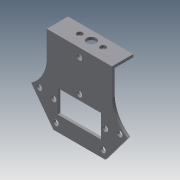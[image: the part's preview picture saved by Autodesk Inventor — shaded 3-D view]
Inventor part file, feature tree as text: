
AUTODESK INVENTOR PART (.ipt)
format: ipt  version: 2013 (Build 170138000, 138)  size: 1,052,160 bytes
history: native  units: mm
features: sketch x94, extrude x83, fillet x2
ambient origin geometry x8: Origin, YZ Plane, XZ Plane, XY Plane, X Axis, Y Axis, Z Axis, Center Point
bodies: Solid1 (feature_tree)
feature tree (179):
  extrude  "Extrusion1"  Depth=10.0mm
  extrude  "Extrusion2"  Depth=10.0mm
  sketch  "Sketch3"  dims[d8=2.0mm d9=0.0mm d11=3.0mm]
  extrude  "Extrusion3"  Depth=3.0mm
  extrude  "Extrusion4"  Depth=3.0mm
  extrude  "Extrusion5"  Depth=10.0mm TaperAngle=0.0deg
  extrude  "Extrusion6"  Depth=3.0mm
  sketch  "Sketch8"  dims[d24=10.0mm d25=0.0mm d26=2.0mm d27=0.0mm]
  extrude  "Extrusion7"  Depth=3.0mm
  extrude  "Extrusion8"  Depth=2.0mm TaperAngle=0.0deg
  extrude  "Extrusion9"  Depth=3.0mm
  extrude  "Extrusion10"  Depth=2.0mm TaperAngle=0.0deg
  extrude  "Extrusion11"  Depth=4.0mm
  extrude  "Extrusion12"  Depth=4.0mm
  extrude  "Extrusion13"  Depth=1.8mm
  sketch  "Sketch16"  dims[d61=4.0mm d62=4.0mm]
  extrude  "Extrusion14"  Depth=4.0mm
  extrude  "Extrusion15"  Depth=12.0mm
  extrude  "Extrusion16"  Depth=4.0mm
  extrude  "Extrusion17"  Depth=16.0mm
  sketch  "Sketch21"  dims[d75=30.0mm d77=2.0mm d78=0.0mm]
  extrude  "Extrusion18"  Depth=10.4mm
  extrude  "Extrusion19"  Depth=4.0mm
  extrude  "Extrusion20"  Depth=20.0mm
  extrude  "Extrusion21"  Depth=2.0mm TaperAngle=0.0deg
  extrude  "Extrusion22"  Depth=2.3mm
  extrude  "Extrusion23"  Depth=24.0mm
  extrude  "Extrusion24"  Depth=2.0mm TaperAngle=0.0deg
  extrude  "Extrusion25"  Depth=3.0mm
  extrude  "Extrusion26"  Depth=2.0mm TaperAngle=0.0deg
  extrude  "Extrusion27"  Depth=2.0mm TaperAngle=0.0deg
  extrude  "Extrusion28"  Depth=4.0mm
  extrude  "Extrusion29"  Depth=3.0mm
  extrude  "Extrusion30"  Depth=3.0mm
  extrude  "Extrusion31"  Depth=3.0mm
  extrude  "Extrusion32"  Depth=4.0mm
  extrude  "Extrusion33"  Depth=3.0mm
  extrude  "Extrusion34"  Depth=2.0mm TaperAngle=0.0deg
  extrude  "Extrusion35"  Depth=2.3mm
  extrude  "Extrusion36"  Depth=4.0mm
  extrude  "Extrusion37"  Depth=2.3mm
  sketch  "Sketch42"  dims[d147=24.0mm d148=24.0mm]
  sketch  "Sketch43"  dims[d149=2.0mm d150=0.0mm d151=2.0mm d152=0.0mm]
  extrude  "Extrusion38"  Depth=2.0mm TaperAngle=0.0deg
  extrude  "Extrusion39"  Depth=2.0mm TaperAngle=0.0deg
  extrude  "Extrusion40"  Depth=20.0mm
  extrude  "Extrusion41"  Depth=20.0mm
  extrude  "Extrusion42"  Depth=24.0mm
  extrude  "Extrusion43"  Depth=2.0mm TaperAngle=0.0deg
  extrude  "Extrusion44"  Depth=3.0mm
  extrude  "Extrusion45"  Depth=20.0mm
  extrude  "Extrusion46"  Depth=2.0mm TaperAngle=0.0deg
  extrude  "Extrusion47"  Depth=3.0mm
  extrude  "Extrusion48"  Depth=3.0mm
  fillet  "Fillet1"  Radius=3.0mm
  extrude  "Extrusion49"  Depth=2.5mm
  fillet  "Fillet2"  Radius=2.0mm
  extrude  "Extrusion50"  Depth=12.5mm
  extrude  "Extrusion51"  Depth=2.5mm
  extrude  "Extrusion52"  Depth=20.0mm
  extrude  "Extrusion53"  Depth=25.0mm
  extrude  "Extrusion54"  Depth=2.0mm TaperAngle=0.0deg
  extrude  "Extrusion55"  Depth=1.5mm
  extrude  "Extrusion56"  Depth=20.0mm
  extrude  "Extrusion57"  Depth=20.0mm
  extrude  "Extrusion58"  Depth=24.0mm
  extrude  "Extrusion59"  Depth=3.4mm
  extrude  "Extrusion60"  Depth=3.0mm
  extrude  "Extrusion61"  Depth=3.0mm
  extrude  "Extrusion62"  Depth=2.0mm TaperAngle=0.0deg
  sketch  "Sketch67"  dims[d218=3.0mm d219=3.0mm]
  extrude  "Extrusion63"  Depth=17.0mm
  extrude  "Extrusion64"  Depth=2.0mm TaperAngle=0.0deg
  extrude  "Extrusion65"  Depth=14.4mm
  sketch  "Sketch71"  dims[d228=1.5mm d229=3.0mm]
  sketch  "Sketch72"  dims[d230=2.0mm d231=0.0mm d233=2.0mm d234=0.0mm]
  extrude  "Extrusion66"  Depth=1.5mm
  sketch  "Sketch73"  dims[d236=14.5mm d237=13.95mm]
  sketch  "Sketch74"  dims[d238=13.95mm d239=3.0mm]
  extrude  "Extrusion67"  Depth=3.0mm
  extrude  "Extrusion68"  Depth=2.0mm TaperAngle=0.0deg
  extrude  "Extrusion69"  Depth=1.5mm
  extrude  "Extrusion70"  Depth=14.4mm
  extrude  "Extrusion71"  Depth=3.0mm
  sketch  "Sketch80"  dims[d256=19.0mm d259=19.0mm]
  sketch  "Sketch81"  dims[d260=2.0mm d261=0.0mm d262=10.0mm]
  extrude  "Extrusion72"  Depth=2.0mm TaperAngle=0.0deg
  extrude  "Extrusion73"  Depth=13.95mm
  sketch  "Sketch84"  dims[d269=2.0mm d270=0.0mm]
  extrude  "Extrusion74"  Depth=3.0mm
  extrude  "Extrusion75"  Depth=2.0mm TaperAngle=0.0deg
  extrude  "Extrusion76"  Depth=14.4mm
  extrude  "Extrusion77"  Depth=2.0mm
  extrude  "Extrusion78"  Depth=4.0mm
  extrude  "Extrusion79"  Depth=2.0mm TaperAngle=0.0deg
  extrude  "Extrusion80"  Depth=19.0mm
  extrude  "Extrusion81"  Depth=10.0mm
  extrude  "Extrusion82"  Depth=4.0mm
  extrude  "Extrusion83"  Depth=2.0mm TaperAngle=0.0deg
  sketch  "Sketch1"  dims[d2=10.0mm d3=10.0mm]
  sketch  "Sketch2"  dims[d4=10.0mm d7=10.0mm]
  sketch  "Sketch4"  dims[d12=3.0mm d14=3.0mm]
  sketch  "Sketch5"  dims[d15=3.0mm d16=10.0mm d17=0.0mm]
  sketch  "Sketch6"  dims[d20=6.0mm d21=3.0mm]
  sketch  "Sketch7"  dims[d22=6.0mm d23=3.0mm]
  sketch  "Sketch9"  dims[d34=3.0mm d36=3.0mm]
  sketch  "Sketch10"  dims[d37=2.0mm d38=0.0mm d39=2.0mm d40=0.0mm]
  sketch  "Sketch11"  dims[d48=2.0mm d49=4.0mm]
  sketch  "Sketch12"  dims[d51=12.0mm d52=4.0mm]
  sketch  "Sketch13"  dims[d53=2.0mm d54=0.0mm d55=1.8mm]
  sketch  "Sketch14"  dims[d56=2.0mm d57=4.0mm]
  sketch  "Sketch15"  dims[d58=2.0mm d59=0.0mm d60=12.0mm]
  sketch  "Sketch17"  dims[d63=2.0mm d64=0.0mm d65=16.0mm]
  sketch  "Sketch18"  dims[d66=12.0mm d67=10.4mm]
  sketch  "Sketch19"  dims[d68=2.0mm d69=0.0mm d70=4.0mm]
  sketch  "Sketch20"  dims[d71=2.0mm d72=0.0mm d74=20.0mm]
  sketch  "Sketch22"  dims[d83=2.3mm d84=2.3mm]
  sketch  "Sketch23"  dims[d85=2.0mm d86=0.0mm d90=24.0mm]
  sketch  "Sketch24"  dims[d92=24.0mm d93=2.0mm d94=0.0mm]
  sketch  "Sketch25"  dims[d97=3.0mm d98=3.0mm]
  sketch  "Sketch26"  dims[d100=3.0mm d101=2.0mm d102=0.0mm]
  sketch  "Sketch27"  dims[d103=2.0mm d104=0.0mm d105=2.0mm d106=0.0mm]
  sketch  "Sketch28"  dims[d111=4.0mm d112=4.0mm]
  sketch  "Sketch29"  dims[d113=3.0mm d114=3.0mm]
  sketch  "Sketch30"  dims[d116=3.0mm d117=3.0mm]
  sketch  "Sketch31"  dims[d118=3.0mm d119=3.0mm]
  sketch  "Sketch32"  dims[d120=3.0mm d121=4.0mm]
  sketch  "Sketch33"  dims[d122=3.0mm d123=3.0mm]
  sketch  "Sketch34"  dims[d124=3.0mm d125=2.0mm d126=0.0mm]
  sketch  "Sketch35"  dims[d127=2.3mm d128=2.3mm]
  sketch  "Sketch36"  dims[d131=4.0mm d132=4.0mm]
  sketch  "Sketch37"  dims[d133=2.0mm d134=0.0mm d135=2.3mm]
  sketch  "Sketch38"  dims[d136=2.3mm d137=2.0mm d138=0.0mm]
  sketch  "Sketch39"  dims[d139=3.0mm d140=2.0mm d141=0.0mm]
  sketch  "Sketch40"  dims[d142=2.0mm d143=0.0mm d144=20.0mm]
  sketch  "Sketch41"  dims[d145=14.0mm d146=20.0mm]
  sketch  "Sketch44"  dims[d157=3.0mm d158=3.0mm]
  sketch  "Sketch45"  dims[d159=2.0mm d160=0.0mm d161=20.0mm]
  sketch  "Sketch46"  dims[d162=20.0mm d163=2.0mm d164=0.0mm]
  sketch  "Sketch47"  dims[d165=2.0mm d166=0.0mm d167=3.0mm]
  sketch  "Sketch48"  dims[d168=3.0mm d169=3.0mm d170=3.0mm]
  sketch  "Sketch49"  dims[d171=2.5mm d172=2.5mm d173=2.0mm d174=0.0mm]
  sketch  "Sketch50"  dims[d175=2.0mm d176=0.0mm d178=12.5mm]
  sketch  "Sketch51"  dims[d179=12.5mm d180=2.5mm]
  sketch  "Sketch52"  dims[d181=2.5mm d183=20.0mm]
  sketch  "Sketch53"  dims[d185=20.0mm d186=25.0mm]
  sketch  "Sketch54"  dims[d187=25.0mm d188=2.0mm d189=0.0mm]
  sketch  "Sketch55"  dims[d190=1.5mm d191=1.5mm]
  sketch  "Sketch56"  dims[d192=1.5mm d193=20.0mm]
  sketch  "Sketch57"  dims[d194=1.5mm d195=20.0mm]
  sketch  "Sketch58"  dims[d196=24.0mm d197=24.0mm]
  sketch  "Sketch59"  dims[d198=2.0mm d199=0.0mm d200=3.4mm]
  sketch  "Sketch60"  dims[d201=3.4mm d202=3.0mm]
  sketch  "Sketch61"  dims[d203=3.0mm d204=3.0mm]
  sketch  "Sketch62"  dims[d205=3.0mm d206=2.0mm d207=0.0mm]
  sketch  "Sketch63"  dims[d208=2.0mm d209=0.0mm d210=17.0mm]
  sketch  "Sketch64"  dims[d211=14.4mm d212=2.0mm d213=0.0mm]
  sketch  "Sketch65"  dims[d214=19.5mm d215=14.4mm]
  sketch  "Sketch66"  dims[d216=1.5mm d217=1.5mm]
  sketch  "Sketch68"  dims[d220=2.0mm d221=0.0mm d222=2.0mm d223=0.0mm]
  sketch  "Sketch69"  dims[d224=19.5mm d225=1.5mm]
  sketch  "Sketch70"  dims[d226=3.0mm d227=14.4mm]
  sketch  "Sketch75"  dims[d241=3.0mm d242=2.0mm d243=0.0mm]
  sketch  "Sketch76"  dims[d244=2.0mm d245=0.0mm d248=14.4mm]
  sketch  "Sketch77"  dims[d249=21.6mm d250=2.0mm]
  sketch  "Sketch78"  dims[d251=2.0mm d252=4.0mm]
  sketch  "Sketch79"  dims[d253=4.0mm d254=2.0mm d255=0.0mm]
  sketch  "Sketch82"  dims[d263=4.0mm d264=4.0mm]
  sketch  "Sketch83"  dims[d265=2.0mm d266=0.0mm d267=2.0mm d268=0.0mm]
  sketch  "Sketch85"  dims[d271=2.0mm d272=0.0mm]
  sketch  "Sketch86"  dims[d273=3.6mm]
  sketch  "Sketch87"  dims[d274=2.0mm d275=0.0mm]
  sketch  "Sketch88"  dims[d276=1.5mm]
  sketch  "Sketch89"  dims[d277=10.0mm d278=0.0mm]
  sketch  "Sketch90"  dims[d279=2.0mm]
  sketch  "Sketch91"  dims[d280=0.5mm d281=0.0mm]
  sketch  "Sketch92"  dims[d282=0.5mm]
  sketch  "Sketch93"  dims[d283=1.5mm d284=0.0mm]
  sketch  "Sketch94"  dims[d285=1.5mm d286=0.0mm d287=10.4mm d288=14.398895mm d289=16.0mm d290=1.5mm d291=0.0mm d292=1.5mm d293=0.0mm d294=10.0mm d295=0.0mm d296=10.0mm d297=0.0mm d298=10.0mm d299=0.0mm d300=20.0mm d301=0.0mm d306=1.5mm d307=0.0mm d308=4.0mm d309=7.0mm d310=16.0mm d311=3.0mm d312=7.0mm d313=16.0mm d314=1.5mm d315=0.0mm d316=5.0mm d317=1.5mm d318=0.0mm d319=1.5mm d320=10.0mm d321=0.0mm d322=7.0mm d323=7.0mm d324=4.0mm d325=7.0mm d326=4.0mm d327=7.0mm d328=4.0mm d329=1.5mm d330=0.0mm d331=4.0mm d332=4.129mm d333=7.0mm d335=3.072mm d336=7.0mm d337=15.0mm d338=1.5mm d339=0.0mm d341=1.5mm d342=0.0mm d343=0.5mm d344=7.0mm d345=18.0mm d346=7.0mm d347=1.5mm d348=0.0mm d349=7.0mm d351=7.0mm d353=1.5mm d354=0.0mm d359=8.3mm d360=11.6mm d361=23.6mm d362=12.4mm d363=1.5mm d364=0.0mm d365=27.9mm d366=0.4mm d367=1.5mm d368=0.0mm d370=0.3mm d371=0.3mm d372=1.5mm d373=0.0mm d374=5.0mm d375=5.0mm d376=1.5mm d377=0.0mm d378=6.3mm d379=12.6mm d380=3.0mm d381=3.0mm d382=1.5mm d383=0.0mm d391=1.5mm d392=0.0mm d395=7.0mm d396=19.0mm d399=7.0mm d400=1.5mm d401=0.0mm d403=1.5mm d404=0.0mm d406=1.5mm d407=3.0mm d409=1.5mm d410=3.0mm d411=1.5mm d412=0.0mm d413=14.5mm d414=3.0mm d415=1.5mm d416=0.0mm d417=3.0mm d418=1.5mm d419=3.0mm d420=2.0mm d421=3.0mm d422=3.0mm d423=1.5mm d424=0.0mm d425=1.5mm d426=1.5mm d427=0.0mm d428=1.5mm d429=1.5mm d430=0.0mm d431=1.5mm d432=0.0mm d433=3.0mm d434=3.0mm d435=3.0mm d436=3.0mm d437=1.5mm d438=0.0mm d439=1.5mm d440=0.0mm d441=3.0mm d442=3.0mm d443=1.5mm d444=0.0mm]
